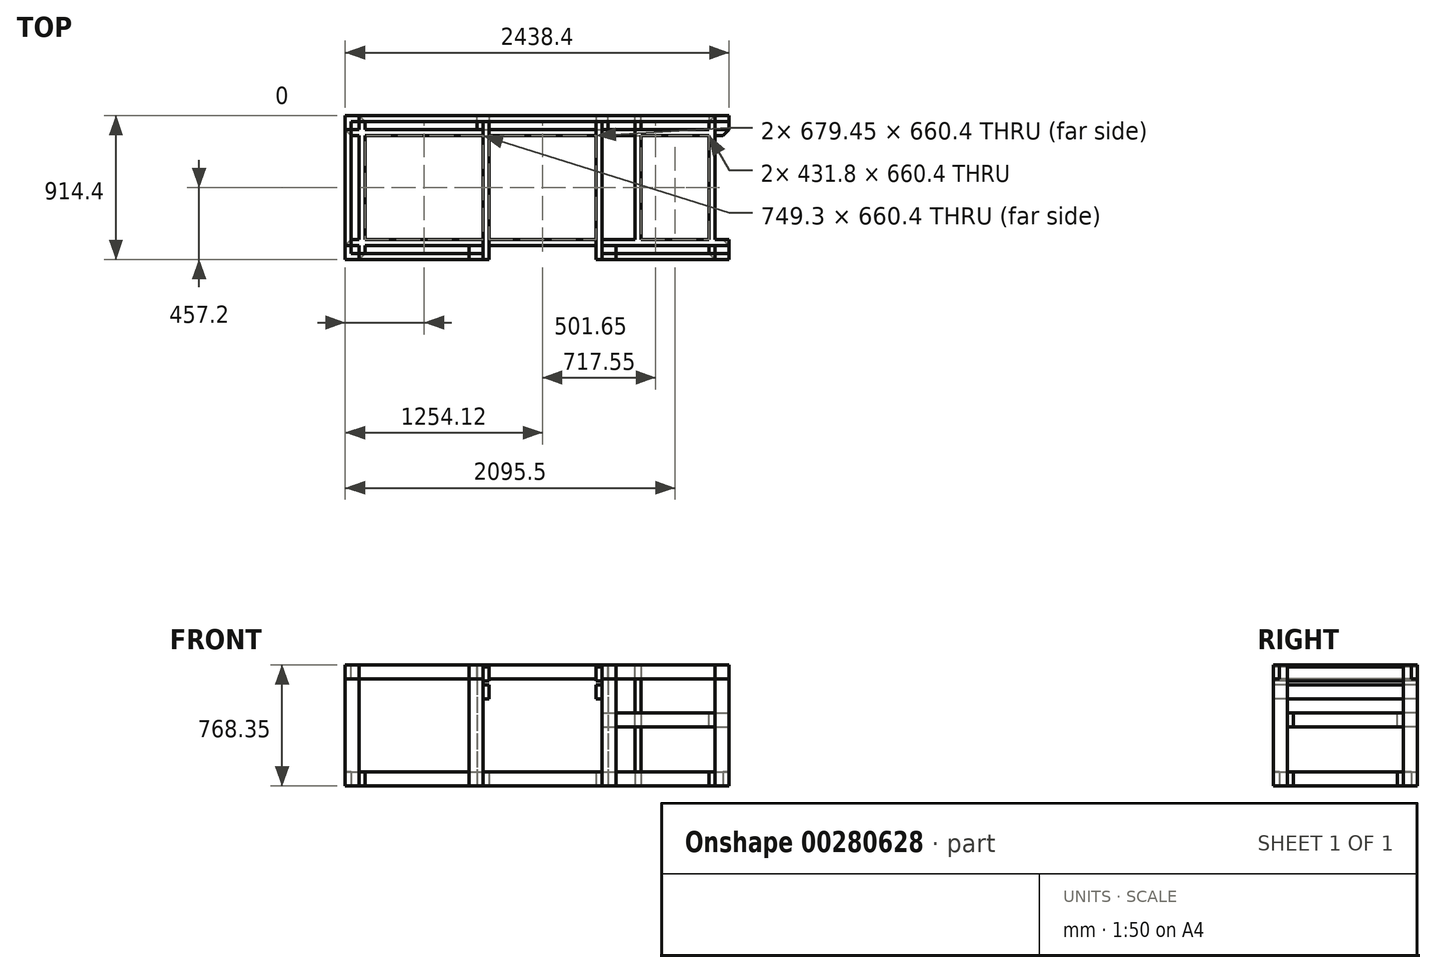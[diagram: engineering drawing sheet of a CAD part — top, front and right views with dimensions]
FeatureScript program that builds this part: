
annotation { "Feature Type Name" : "Feature", "Feature Type Description" : "" }
export const myFeature = defineFeature(function(context is Context, id is Id, definition is map)
    precondition{}
    {
        {
            var Q0;
            Q0=qCreatedBy(makeId("Top.planeOp"),FACE);
            var sketch = newSketch(context, id + "F0", { "sketchPlane" : qUnion([Q0])});
            skLineSegment(sketch, "E0.bottom", {"start": v(-1219.2, -457.2) * mm, "end": v(-1130.3, -457.2) * mm});
            skLineSegment(sketch, "E0.top", {"start": v(-1219.2, -368.3) * mm, "end": v(-1130.3, -368.3) * mm});
            skLineSegment(sketch, "E0.left", {"start": v(-1219.2, -457.2) * mm, "end": v(-1219.2, -368.3) * mm});
            skLineSegment(sketch, "E0.right", {"start": v(-1130.3, -457.2) * mm, "end": v(-1130.3, -368.3) * mm});
            skLineSegment(sketch, "E1.0.1.0", {"start": v(-1219.2, 457.2) * mm, "end": v(-1130.3, 457.2) * mm});
            skLineSegment(sketch, "E1.0.1.1", {"start": v(-1130.3, 368.3) * mm, "end": v(-1130.3, 457.2) * mm});
            skLineSegment(sketch, "E1.0.1.2", {"start": v(-1219.2, 368.3) * mm, "end": v(-1130.3, 368.3) * mm});
            skLineSegment(sketch, "E1.0.1.3", {"start": v(-1219.2, 368.3) * mm, "end": v(-1219.2, 457.2) * mm});
            skLineSegment(sketch, "E1.1.0.0", {"start": v(1130.3, -368.3) * mm, "end": v(1219.2, -368.3) * mm});
            skLineSegment(sketch, "E1.1.0.1", {"start": v(1219.2, -457.2) * mm, "end": v(1219.2, -368.3) * mm});
            skLineSegment(sketch, "E1.1.0.2", {"start": v(1130.3, -457.2) * mm, "end": v(1219.2, -457.2) * mm});
            skLineSegment(sketch, "E1.1.0.3", {"start": v(1130.3, -457.2) * mm, "end": v(1130.3, -368.3) * mm});
            skLineSegment(sketch, "E1.1.1.0", {"start": v(1130.3, 457.2) * mm, "end": v(1219.2, 457.2) * mm});
            skLineSegment(sketch, "E1.1.1.1", {"start": v(1219.2, 368.3) * mm, "end": v(1219.2, 457.2) * mm});
            skLineSegment(sketch, "E1.1.1.2", {"start": v(1130.3, 368.3) * mm, "end": v(1219.2, 368.3) * mm});
            skLineSegment(sketch, "E1.1.1.3", {"start": v(1130.3, 368.3) * mm, "end": v(1130.3, 457.2) * mm});
            skLineSegment(sketch, "E1.direction1", {"start": v(-1219.2, -457.2) * mm, "end": v(1130.3, -457.2) * mm, "construction": true});
            skLineSegment(sketch, "E1.direction2", {"start": v(-1219.2, -457.2) * mm, "end": v(-1219.2, 368.3) * mm, "construction": true});
            skLineSegment(sketch, "E2.bottom", {"start": v(-431.8, -457.2) * mm, "end": v(-342.9, -457.2) * mm});
            skLineSegment(sketch, "E2.top", {"start": v(-431.8, -368.3) * mm, "end": v(-342.9, -368.3) * mm});
            skLineSegment(sketch, "E2.left", {"start": v(-431.8, -457.2) * mm, "end": v(-431.8, -368.3) * mm});
            skLineSegment(sketch, "E2.right", {"start": v(-342.9, -457.2) * mm, "end": v(-342.9, -368.3) * mm});
            skLineSegment(sketch, "E3.bottom", {"start": v(412.75, -457.2) * mm, "end": v(501.65, -457.2) * mm});
            skLineSegment(sketch, "E3.top", {"start": v(412.75, -368.3) * mm, "end": v(501.65, -368.3) * mm});
            skLineSegment(sketch, "E3.left", {"start": v(412.75, -457.2) * mm, "end": v(412.75, -368.3) * mm});
            skLineSegment(sketch, "E3.right", {"start": v(501.65, -457.2) * mm, "end": v(501.65, -368.3) * mm});
            skSolve(sketch);
        }
        {
            var Q0;
            Q0 = qSketchRegion(id + "F0", true);
            extrude(context, id + "F1", {"entities" : qUnion([Q0]), "depth" : 768.35 * mm});
        }
        {
            var Q0;
            Q0=qCreatedBy(makeId("Top.planeOp"),FACE);
            var sketch = newSketch(context, id + "F2", { "sketchPlane" : qUnion([Q0])});
            skLineSegment(sketch, "E4.bottom", {"start": v(-1219.2, 368.3) * mm, "end": v(-1130.3, 368.3) * mm});
            skLineSegment(sketch, "E4.top", {"start": v(-1219.2, 330.2) * mm, "end": v(-1130.3, 330.2) * mm});
            skLineSegment(sketch, "E4.left", {"start": v(-1219.2, 368.3) * mm, "end": v(-1219.2, 330.2) * mm});
            skLineSegment(sketch, "E4.right", {"start": v(1219.2, 368.3) * mm, "end": v(1219.2, 330.2) * mm});
            skLineSegment(sketch, "E5.bottom", {"start": v(-1219.2, -368.3) * mm, "end": v(-1130.3, -368.3) * mm});
            skLineSegment(sketch, "E5.top", {"start": v(-1219.2, -330.2) * mm, "end": v(-1130.3, -330.2) * mm});
            skLineSegment(sketch, "E5.left", {"start": v(-1219.2, -368.3) * mm, "end": v(-1219.2, -330.2) * mm});
            skLineSegment(sketch, "E5.right", {"start": v(1219.2, -368.3) * mm, "end": v(1219.2, -330.2) * mm});
            skLineSegment(sketch, "E6.bottom", {"start": v(-1130.3, -457.2) * mm, "end": v(-1092.2, -457.2) * mm});
            skLineSegment(sketch, "E6.top", {"start": v(-1130.3, 457.2) * mm, "end": v(-1092.2, 457.2) * mm});
            skLineSegment(sketch, "E6.left", {"start": v(-1130.3, -457.2) * mm, "end": v(-1130.3, -368.3) * mm});
            skLineSegment(sketch, "E6.right", {"start": v(-1092.2, -457.2) * mm, "end": v(-1092.2, -368.3) * mm});
            skLineSegment(sketch, "E7.bottom", {"start": v(1130.3, 457.2) * mm, "end": v(1092.2, 457.2) * mm});
            skLineSegment(sketch, "E7.top", {"start": v(1130.3, -457.2) * mm, "end": v(1092.2, -457.2) * mm});
            skLineSegment(sketch, "E7.left", {"start": v(1130.3, 457.2) * mm, "end": v(1130.3, 368.3) * mm});
            skLineSegment(sketch, "E7.right", {"start": v(1092.2, 457.2) * mm, "end": v(1092.2, 368.3) * mm});
            skLineSegment(sketch, "E8.trimOffspring", {"start": v(-1092.2, 368.3) * mm, "end": v(1092.2, 368.3) * mm});
            skLineSegment(sketch, "E9.trimOffspring", {"start": v(-1092.2, 330.2) * mm, "end": v(1092.2, 330.2) * mm});
            skLineSegment(sketch, "E10.trimOffspring", {"start": v(-1130.3, 368.3) * mm, "end": v(-1130.3, 457.2) * mm});
            skLineSegment(sketch, "E11.trimOffspring", {"start": v(-1092.2, 368.3) * mm, "end": v(-1092.2, 457.2) * mm});
            skLineSegment(sketch, "E12.trimOffspring", {"start": v(-1092.2, -330.2) * mm, "end": v(1092.2, -330.2) * mm});
            skLineSegment(sketch, "E13.trimOffspring", {"start": v(-1130.3, -330.2) * mm, "end": v(-1130.3, 330.2) * mm});
            skLineSegment(sketch, "E14.trimOffspring", {"start": v(-1092.2, -368.3) * mm, "end": v(1092.2, -368.3) * mm});
            skLineSegment(sketch, "E15.trimOffspring", {"start": v(-1092.2, -330.2) * mm, "end": v(-1092.2, 330.2) * mm});
            skLineSegment(sketch, "E16.trimOffspring", {"start": v(1130.3, 368.3) * mm, "end": v(1219.2, 368.3) * mm});
            skLineSegment(sketch, "E17.trimOffspring", {"start": v(1092.2, 330.2) * mm, "end": v(1092.2, -330.2) * mm});
            skLineSegment(sketch, "E18.trimOffspring", {"start": v(1130.3, 330.2) * mm, "end": v(1219.2, 330.2) * mm});
            skLineSegment(sketch, "E19.trimOffspring", {"start": v(1130.3, 330.2) * mm, "end": v(1130.3, -330.2) * mm});
            skLineSegment(sketch, "E20.trimOffspring", {"start": v(1130.3, -330.2) * mm, "end": v(1219.2, -330.2) * mm});
            skLineSegment(sketch, "E21.trimOffspring", {"start": v(1092.2, -368.3) * mm, "end": v(1092.2, -457.2) * mm});
            skLineSegment(sketch, "E22.trimOffspring", {"start": v(1130.3, -368.3) * mm, "end": v(1219.2, -368.3) * mm});
            skLineSegment(sketch, "E23.trimOffspring", {"start": v(1130.3, -368.3) * mm, "end": v(1130.3, -457.2) * mm});
            skSolve(sketch);
        }
        {
            var Q0;
            Q0 = qSketchRegion(id + "F2", true);
            extrude(context, id + "F3", {"entities" : qUnion([Q0]), "depth" : 88.9 * mm});
        }
        {
            var Q0;
            Q0=makeQuery(id+"F3.opExtrude","SWEPT_EDGE",EDGE,{"disambiguationData":[OSD([sQuery(id+"F2.wireOp",EDGE,"E4.top"),sQuery(id+"F2.wireOp",EDGE,"E4.left")])]});
            var Q1;
            Q1=makeQuery(id+"F3.opExtrude","SWEPT_EDGE",EDGE,{"disambiguationData":[OSD([sQuery(id+"F2.wireOp",EDGE,"E5.top"),sQuery(id+"F2.wireOp",EDGE,"E5.left")])]});
            var Q2;
            Q2=makeQuery(id+"F3.opExtrude","SWEPT_EDGE",EDGE,{"disambiguationData":[OSD([sQuery(id+"F2.wireOp",EDGE,"E6.bottom"),sQuery(id+"F2.wireOp",EDGE,"E6.right")])]});
            var Q3;
            Q3=makeQuery(id+"F3.opExtrude","SWEPT_EDGE",EDGE,{"disambiguationData":[OSD([sQuery(id+"F2.wireOp",EDGE,"E7.top"),sQuery(id+"F2.wireOp",EDGE,"E21.trimOffspring")])]});
            var Q4;
            Q4=makeQuery(id+"F3.opExtrude","SWEPT_EDGE",EDGE,{"disambiguationData":[OSD([sQuery(id+"F2.wireOp",EDGE,"E4.right"),sQuery(id+"F2.wireOp",EDGE,"E18.trimOffspring")])]});
            var Q5;
            Q5=makeQuery(id+"F3.opExtrude","SWEPT_EDGE",EDGE,{"disambiguationData":[OSD([sQuery(id+"F2.wireOp",EDGE,"E7.bottom"),sQuery(id+"F2.wireOp",EDGE,"E7.right")])]});
            var Q6;
            Q6=makeQuery(id+"F3.opExtrude","SWEPT_EDGE",EDGE,{"disambiguationData":[OSD([sQuery(id+"F2.wireOp",EDGE,"E5.right"),sQuery(id+"F2.wireOp",EDGE,"E20.trimOffspring")])]});
            var Q7;
            Q7=makeQuery(id+"F3.opExtrude","SWEPT_EDGE",EDGE,{"disambiguationData":[OSD([sQuery(id+"F2.wireOp",EDGE,"E6.top"),sQuery(id+"F2.wireOp",EDGE,"E11.trimOffspring")])]});
            chamfer(context, id + "F4", {"entities" : qUnion([Q0, Q1, Q2, Q3, Q4, Q5, Q6, Q7]), "width" : 38.1 * mm, "tangentPropagation" : true});
        }
        {
            var Q0;
            Q0=qCreatedBy(makeId("Top.planeOp"),FACE);
            var sketch = newSketch(context, id + "F5", { "sketchPlane" : qUnion([Q0])});
            skLineSegment(sketch, "E24.bottom", {"start": v(-342.9, 330.2) * mm, "end": v(-304.8, 330.2) * mm});
            skLineSegment(sketch, "E24.top", {"start": v(-342.9, -330.2) * mm, "end": v(-304.8, -330.2) * mm});
            skLineSegment(sketch, "E24.left", {"start": v(-342.9, 330.2) * mm, "end": v(-342.9, -330.2) * mm});
            skLineSegment(sketch, "E24.right", {"start": v(-304.8, 330.2) * mm, "end": v(-304.8, -330.2) * mm});
            skLineSegment(sketch, "E25.bottom", {"start": v(374.65, 330.2) * mm, "end": v(412.75, 330.2) * mm});
            skLineSegment(sketch, "E25.top", {"start": v(374.65, -330.2) * mm, "end": v(412.75, -330.2) * mm});
            skLineSegment(sketch, "E25.left", {"start": v(374.65, 330.2) * mm, "end": v(374.65, -330.2) * mm});
            skLineSegment(sketch, "E25.right", {"start": v(412.75, 330.2) * mm, "end": v(412.75, -330.2) * mm});
            skSolve(sketch);
        }
        {
            var Q0;
            Q0 = qSketchRegion(id + "F5", true);
            var Q1;
            Q1=makeQuery(id+"F3.opExtrude","CAP_FACE",FACE,{"disambiguationData":[OSD([sQuery(id+"F2.wireOp",EDGE,"E4.bottom"),sQuery(id+"F2.wireOp",EDGE,"E4.top"),sQuery(id+"F2.wireOp",EDGE,"E4.left"),sQuery(id+"F2.wireOp",EDGE,"E4.right"),sQuery(id+"F2.wireOp",EDGE,"E5.bottom"),sQuery(id+"F2.wireOp",EDGE,"E5.top"),sQuery(id+"F2.wireOp",EDGE,"E5.left"),sQuery(id+"F2.wireOp",EDGE,"E5.right"),sQuery(id+"F2.wireOp",EDGE,"E6.bottom"),sQuery(id+"F2.wireOp",EDGE,"E6.top"),sQuery(id+"F2.wireOp",EDGE,"E6.left"),sQuery(id+"F2.wireOp",EDGE,"E6.right"),sQuery(id+"F2.wireOp",EDGE,"E7.bottom"),sQuery(id+"F2.wireOp",EDGE,"E7.top"),sQuery(id+"F2.wireOp",EDGE,"E7.left"),sQuery(id+"F2.wireOp",EDGE,"E7.right"),sQuery(id+"F2.wireOp",EDGE,"E8.trimOffspring"),sQuery(id+"F2.wireOp",EDGE,"E9.trimOffspring"),sQuery(id+"F2.wireOp",EDGE,"E10.trimOffspring"),sQuery(id+"F2.wireOp",EDGE,"E11.trimOffspring"),sQuery(id+"F2.wireOp",EDGE,"E12.trimOffspring"),sQuery(id+"F2.wireOp",EDGE,"E13.trimOffspring"),sQuery(id+"F2.wireOp",EDGE,"E14.trimOffspring"),sQuery(id+"F2.wireOp",EDGE,"E15.trimOffspring"),sQuery(id+"F2.wireOp",EDGE,"E16.trimOffspring"),sQuery(id+"F2.wireOp",EDGE,"E17.trimOffspring"),sQuery(id+"F2.wireOp",EDGE,"E18.trimOffspring"),sQuery(id+"F2.wireOp",EDGE,"E19.trimOffspring"),sQuery(id+"F2.wireOp",EDGE,"E20.trimOffspring"),sQuery(id+"F2.wireOp",EDGE,"E21.trimOffspring"),sQuery(id+"F2.wireOp",EDGE,"E22.trimOffspring"),sQuery(id+"F2.wireOp",EDGE,"E23.trimOffspring")])],"isStart":false});
            extrude(context, id + "F6", {"entities" : qUnion([Q0]), "operationType" : NewBodyOperationType.ADD, "endBound" : BoundingType.UP_TO_SURFACE, "endBoundEntityFace" : qUnion([Q1]), "depth" : 25.4 * mm});
        }
        {
            var Q0;
            Q0=qCreatedBy(makeId("Top.planeOp"),FACE);
            var sketch = newSketch(context, id + "F7", { "sketchPlane" : qUnion([Q0])});
            skLineSegment(sketch, "E26.bottom", {"start": v(-342.9, 457.2) * mm, "end": v(-381, 457.2) * mm});
            skLineSegment(sketch, "E26.top", {"start": v(-342.9, 368.3) * mm, "end": v(-381, 368.3) * mm});
            skLineSegment(sketch, "E26.left", {"start": v(-342.9, 457.2) * mm, "end": v(-342.9, 368.3) * mm});
            skLineSegment(sketch, "E26.right", {"start": v(-381, 457.2) * mm, "end": v(-381, 368.3) * mm});
            skLineSegment(sketch, "E27.bottom", {"start": v(450.85, 457.2) * mm, "end": v(412.75, 457.2) * mm});
            skLineSegment(sketch, "E27.top", {"start": v(412.75, 368.3) * mm, "end": v(450.85, 368.3) * mm});
            skLineSegment(sketch, "E27.left", {"start": v(450.85, 457.2) * mm, "end": v(450.85, 368.3) * mm});
            skLineSegment(sketch, "E27.right", {"start": v(412.75, 457.2) * mm, "end": v(412.75, 368.3) * mm});
            skLineSegment(sketch, "E28.bottom", {"start": v(622.3, 457.2) * mm, "end": v(660.4, 457.2) * mm});
            skLineSegment(sketch, "E28.top", {"start": v(622.3, 368.3) * mm, "end": v(660.4, 368.3) * mm});
            skLineSegment(sketch, "E28.left", {"start": v(622.3, 457.2) * mm, "end": v(622.3, 368.3) * mm});
            skLineSegment(sketch, "E28.right", {"start": v(660.4, 457.2) * mm, "end": v(660.4, 368.3) * mm});
            skSolve(sketch);
        }
        {
            var Q0;
            Q0 = qSketchRegion(id + "F7", true);
            var Q1;
            Q1=makeQuery(id+"F1.opExtrude","CAP_FACE",FACE,{"disambiguationData":[OSD([sQuery(id+"F0.wireOp",EDGE,"E1.0.1.0"),sQuery(id+"F0.wireOp",EDGE,"E1.0.1.1"),sQuery(id+"F0.wireOp",EDGE,"E1.0.1.2"),sQuery(id+"F0.wireOp",EDGE,"E1.0.1.3")])],"isStart":false});
            extrude(context, id + "F8", {"entities" : qUnion([Q0]), "operationType" : NewBodyOperationType.ADD, "endBound" : BoundingType.UP_TO_SURFACE, "endBoundEntityFace" : qUnion([Q1]), "depth" : 25.4 * mm});
        }
        {
            var Q0;
            Q0=makeQuery(id+"F1.opExtrude","CAP_FACE",FACE,{"disambiguationData":[OSD([sQuery(id+"F0.wireOp",EDGE,"E0.bottom"),sQuery(id+"F0.wireOp",EDGE,"E0.top"),sQuery(id+"F0.wireOp",EDGE,"E0.left"),sQuery(id+"F0.wireOp",EDGE,"E0.right")])],"isStart":false});
            cPlane(context, id + "F9", {"entities" : qUnion([Q0]), "cplaneType" : CPlaneType.OFFSET, "offset" : 127 * mm, "oppositeDirection" : true, "width" : 152.4 * mm, "height" : 152.4 * mm});
        }
        {
            var Q0;
            Q0=qCreatedBy(id+"F9.planeOp",FACE);
            cPlane(context, id + "F10", {"entities" : qUnion([Q0]), "cplaneType" : CPlaneType.OFFSET, "offset" : 25.4 * mm, "width" : 152.4 * mm, "height" : 152.4 * mm});
        }
        {
            var Q0;
            Q0=makeQuery(id+"F1.opExtrude","CAP_FACE",FACE,{"disambiguationData":[OSD([sQuery(id+"F0.wireOp",EDGE,"E1.1.1.0"),sQuery(id+"F0.wireOp",EDGE,"E1.1.1.1"),sQuery(id+"F0.wireOp",EDGE,"E1.1.1.2"),sQuery(id+"F0.wireOp",EDGE,"E1.1.1.3")])],"isStart":false});
            cPlane(context, id + "F11", {"entities" : qUnion([Q0]), "cplaneType" : CPlaneType.OFFSET, "offset" : 304.8 * mm, "oppositeDirection" : true, "width" : 152.4 * mm, "height" : 152.4 * mm});
        }
        {
            var Q0;
            Q0=makeQuery(id+"F1.opExtrude","CAP_FACE",FACE,{"disambiguationData":[OSD([sQuery(id+"F0.wireOp",EDGE,"E0.bottom"),sQuery(id+"F0.wireOp",EDGE,"E0.top"),sQuery(id+"F0.wireOp",EDGE,"E0.left"),sQuery(id+"F0.wireOp",EDGE,"E0.right")])],"isStart":false});
            var sketch = newSketch(context, id + "F12", { "sketchPlane" : qUnion([Q0])});
            skLineSegment(sketch, "E29.bottom", {"start": v(-1219.2, 457.2) * mm, "end": v(1219.2, 457.2) * mm});
            skLineSegment(sketch, "E29.top", {"start": v(-1181.1, 419.1) * mm, "end": v(1219.2, 419.1) * mm});
            skLineSegment(sketch, "E29.left", {"start": v(-1219.2, 457.2) * mm, "end": v(-1219.2, 419.1) * mm});
            skLineSegment(sketch, "E29.right", {"start": v(1219.2, 457.2) * mm, "end": v(1219.2, 419.1) * mm});
            skLineSegment(sketch, "E30.top", {"start": v(-1181.1, -457.2) * mm, "end": v(-1219.2, -457.2) * mm});
            skLineSegment(sketch, "E30.left", {"start": v(-1181.1, 419.1) * mm, "end": v(-1181.1, -419.1) * mm});
            skLineSegment(sketch, "E30.right", {"start": v(-1219.2, 419.1) * mm, "end": v(-1219.2, -457.2) * mm});
            skLineSegment(sketch, "E31.bottom", {"start": v(-1181.1, -419.1) * mm, "end": v(-342.9, -419.1) * mm});
            skLineSegment(sketch, "E31.top", {"start": v(-1181.1, -457.2) * mm, "end": v(-342.9, -457.2) * mm});
            skLineSegment(sketch, "E31.right", {"start": v(-342.9, -419.1) * mm, "end": v(-342.9, -457.2) * mm});
            skLineSegment(sketch, "E32.bottom", {"start": v(412.75, -419.1) * mm, "end": v(1219.2, -419.1) * mm});
            skLineSegment(sketch, "E32.top", {"start": v(412.75, -457.2) * mm, "end": v(1219.2, -457.2) * mm});
            skLineSegment(sketch, "E32.left", {"start": v(412.75, -419.1) * mm, "end": v(412.75, -457.2) * mm});
            skLineSegment(sketch, "E32.right", {"start": v(1219.2, -419.1) * mm, "end": v(1219.2, -457.2) * mm});
            skSolve(sketch);
        }
        {
            var Q0;
            Q0=qCreatedBy(id+"F11.planeOp",FACE);
            var sketch = newSketch(context, id + "F13", { "sketchPlane" : qUnion([Q0])});
            skLineSegment(sketch, "E33.bottom", {"start": v(412.75, -330.2) * mm, "end": v(1219.2, -330.2) * mm});
            skLineSegment(sketch, "E33.top", {"start": v(412.75, -368.3) * mm, "end": v(1219.2, -368.3) * mm});
            skLineSegment(sketch, "E33.left", {"start": v(412.75, -330.2) * mm, "end": v(412.75, -368.3) * mm});
            skLineSegment(sketch, "E33.right", {"start": v(1219.2, -330.2) * mm, "end": v(1219.2, -368.3) * mm});
            skLineSegment(sketch, "E34.bottom", {"start": v(1092.2, 457.2) * mm, "end": v(1130.3, 457.2) * mm});
            skLineSegment(sketch, "E34.top", {"start": v(1092.2, -330.2) * mm, "end": v(1130.3, -330.2) * mm});
            skLineSegment(sketch, "E34.left", {"start": v(1092.2, 457.2) * mm, "end": v(1092.2, -330.2) * mm});
            skLineSegment(sketch, "E34.right", {"start": v(1130.3, 457.2) * mm, "end": v(1130.3, -330.2) * mm});
            skLineSegment(sketch, "E35.bottom", {"start": v(622.3, 368.3) * mm, "end": v(1092.2, 368.3) * mm});
            skLineSegment(sketch, "E35.top", {"start": v(622.3, 330.2) * mm, "end": v(1092.2, 330.2) * mm});
            skLineSegment(sketch, "E35.left", {"start": v(622.3, 368.3) * mm, "end": v(622.3, 330.2) * mm});
            skLineSegment(sketch, "E35.right", {"start": v(1092.2, 368.3) * mm, "end": v(1092.2, 330.2) * mm});
            skLineSegment(sketch, "E36.bottom", {"start": v(622.3, 330.2) * mm, "end": v(660.4, 330.2) * mm});
            skLineSegment(sketch, "E36.top", {"start": v(622.3, -330.2) * mm, "end": v(660.4, -330.2) * mm});
            skLineSegment(sketch, "E36.left", {"start": v(622.3, 330.2) * mm, "end": v(622.3, -330.2) * mm});
            skLineSegment(sketch, "E36.right", {"start": v(660.4, 330.2) * mm, "end": v(660.4, -330.2) * mm});
            skSolve(sketch);
        }
        {
            var Q0;
            Q0 = qSketchRegion(id + "F13", true);
            extrude(context, id + "F14", {"entities" : qUnion([Q0]), "oppositeDirection" : true, "depth" : 88.9 * mm});
        }
        {
            var Q0;
            Q0=qCreatedBy(id+"F9.planeOp",FACE);
            var sketch = newSketch(context, id + "F15", { "sketchPlane" : qUnion([Q0])});
            skLineSegment(sketch, "E37.bottom", {"start": v(-342.9, 457.2) * mm, "end": v(-304.8, 457.2) * mm});
            skLineSegment(sketch, "E37.top", {"start": v(-342.9, -457.2) * mm, "end": v(-304.8, -457.2) * mm});
            skLineSegment(sketch, "E37.left", {"start": v(-342.9, 457.2) * mm, "end": v(-342.9, -457.2) * mm});
            skLineSegment(sketch, "E37.right", {"start": v(-304.8, 457.2) * mm, "end": v(-304.8, -457.2) * mm});
            skLineSegment(sketch, "E38.bottom", {"start": v(374.65, 457.2) * mm, "end": v(412.75, 457.2) * mm});
            skLineSegment(sketch, "E38.top", {"start": v(374.65, -457.2) * mm, "end": v(412.75, -457.2) * mm});
            skLineSegment(sketch, "E38.left", {"start": v(374.65, 457.2) * mm, "end": v(374.65, -457.2) * mm});
            skLineSegment(sketch, "E38.right", {"start": v(412.75, 457.2) * mm, "end": v(412.75, -457.2) * mm});
            skSolve(sketch);
        }
        {
            var Q0;
            Q0 = qSketchRegion(id + "F15", true);
            extrude(context, id + "F16", {"entities" : qUnion([Q0]), "oppositeDirection" : true, "depth" : 88.9 * mm});
        }
        {
            var Q0;
            Q0=qCreatedBy(id+"F10.planeOp",FACE);
            var sketch = newSketch(context, id + "F17", { "sketchPlane" : qUnion([Q0])});
            skLineSegment(sketch, "E39.bottom", {"start": v(-342.9, 457.2) * mm, "end": v(-304.8, 457.2) * mm});
            skLineSegment(sketch, "E39.top", {"start": v(-342.9, -457.2) * mm, "end": v(-304.8, -457.2) * mm});
            skLineSegment(sketch, "E39.left", {"start": v(-342.9, 457.2) * mm, "end": v(-342.9, -457.2) * mm});
            skLineSegment(sketch, "E39.right", {"start": v(-304.8, 457.2) * mm, "end": v(-304.8, -457.2) * mm});
            skLineSegment(sketch, "E40.bottom", {"start": v(374.65, 457.2) * mm, "end": v(412.75, 457.2) * mm});
            skLineSegment(sketch, "E40.top", {"start": v(374.65, -457.2) * mm, "end": v(412.75, -457.2) * mm});
            skLineSegment(sketch, "E40.left", {"start": v(374.65, 457.2) * mm, "end": v(374.65, -457.2) * mm});
            skLineSegment(sketch, "E40.right", {"start": v(412.75, 457.2) * mm, "end": v(412.75, -457.2) * mm});
            skSolve(sketch);
        }
        {
            var Q0;
            Q0 = qSketchRegion(id + "F17", true);
            extrude(context, id + "F18", {"entities" : qUnion([Q0]), "depth" : 88.9 * mm});
        }
        {
            var Q0;
            Q0 = qSketchRegion(id + "F12", true);
            extrude(context, id + "F19", {"entities" : qUnion([Q0]), "oppositeDirection" : true, "depth" : 88.9 * mm});
        }
    });
